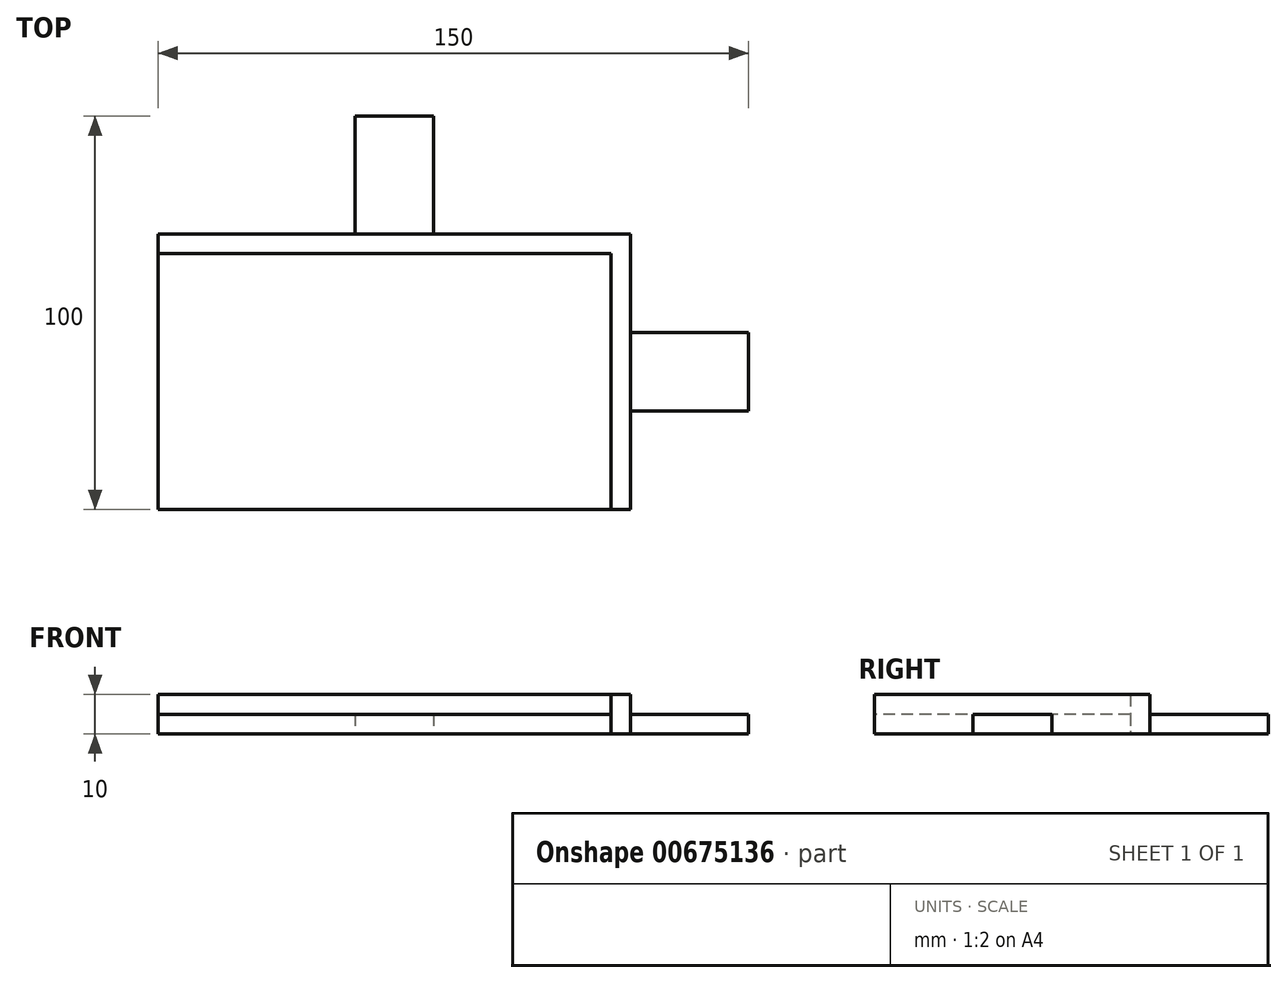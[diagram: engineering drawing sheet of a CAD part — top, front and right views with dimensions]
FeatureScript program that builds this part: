
annotation { "Feature Type Name" : "Feature", "Feature Type Description" : "" }
export const myFeature = defineFeature(function(context is Context, id is Id, definition is map)
    precondition{}
    {
        {
            var Q0;
            Q0=qCreatedBy(makeId("Top.planeOp"),FACE);
            var sketch = newSketch(context, id + "F0", { "sketchPlane" : qUnion([Q0])});
            skLineSegment(sketch, "E0.bottom", {"start": v(0, 0) * mm, "end": v(-120, 0) * mm});
            skLineSegment(sketch, "E0.top", {"start": v(0, 70) * mm, "end": v(-120, 70) * mm});
            skLineSegment(sketch, "E0.left", {"start": v(0, 0) * mm, "end": v(0, 70) * mm});
            skLineSegment(sketch, "E0.right", {"start": v(-120, 0) * mm, "end": v(-120, 70) * mm});
            skLineSegment(sketch, "E1", {"start": v(-5, 65) * mm, "end": v(-120, 65) * mm});
            skLineSegment(sketch, "E2", {"start": v(-5, 65) * mm, "end": v(-5, 0) * mm});
            skLineSegment(sketch, "E3", {"start": v(30, 35) * mm, "end": v(30, 45) * mm});
            skLineSegment(sketch, "E4", {"start": v(30, 45) * mm, "end": v(0, 45) * mm});
            skLineSegment(sketch, "E5.MirrorCS", {"start": v(30, 25) * mm, "end": v(0, 25) * mm});
            skLineSegment(sketch, "E6.MirrorCS", {"start": v(30, 35) * mm, "end": v(30, 25) * mm});
            skPoint(sketch, "E7.start.orphan", {"position": v(0, 35) * mm});
            skLineSegment(sketch, "E8", {"start": v(-60, 100) * mm, "end": v(-50, 100) * mm});
            skLineSegment(sketch, "E9", {"start": v(-50, 100) * mm, "end": v(-50, 70) * mm});
            skLineSegment(sketch, "E10.MirrorCS", {"start": v(-70, 100) * mm, "end": v(-70, 70) * mm});
            skLineSegment(sketch, "E11.MirrorCS", {"start": v(-60, 100) * mm, "end": v(-70, 100) * mm});
            skPoint(sketch, "E12.start.orphan", {"position": v(-60, 70) * mm});
            skSolve(sketch);
        }
        {
            var Q0;
            {var subQ4=sQuery(id+"F0.wireOp",EDGE,"E1");Q0=makeQuery(id+"F0.imprint","IMPRINT",FACE,{"disambiguationData":[TD([[makeQuery(id+"F0.imprint","IMPRINT",EDGE,{"derivedFrom":subQ4}),1.0]])]});}
            extrude(context, id + "F1", {"entities" : qUnion([Q0]), "depth" : 5 * mm, "offsetDistance" : 25 * mm});
        }
        {
            var Q0;
            Q0=makeQuery(id+"F0.imprint","IMPRINT",FACE,{"disambiguationData":[TD([[makeQuery(id+"F0.imprint","IMPRINT",EDGE,{"derivedFrom":sQuery(id+"F0.wireOp",EDGE,"E8")}),-1.0]])]});
            var Q1;
            Q1=makeQuery(id+"F0.imprint","IMPRINT",FACE,{"disambiguationData":[TD([[makeQuery(id+"F0.imprint","IMPRINT",EDGE,{"derivedFrom":sQuery(id+"F0.wireOp",EDGE,"E3")}),1.0]])]});
            extrude(context, id + "F2", {"entities" : qUnion([Q0, Q1]), "depth" : 5 * mm, "offsetDistance" : 25 * mm});
        }
        {
            var Q0;
            {var subQ12=sQuery(id+"F0.wireOp",EDGE,"E1");Q0=makeQuery(id+"F0.imprint","IMPRINT",FACE,{"disambiguationData":[TD([[makeQuery(id+"F0.imprint","IMPRINT",EDGE,{"derivedFrom":subQ12}),-1.0]])]});}
            extrude(context, id + "F3", {"entities" : qUnion([Q0]), "depth" : 10 * mm, "offsetDistance" : 25 * mm});
        }
    });
